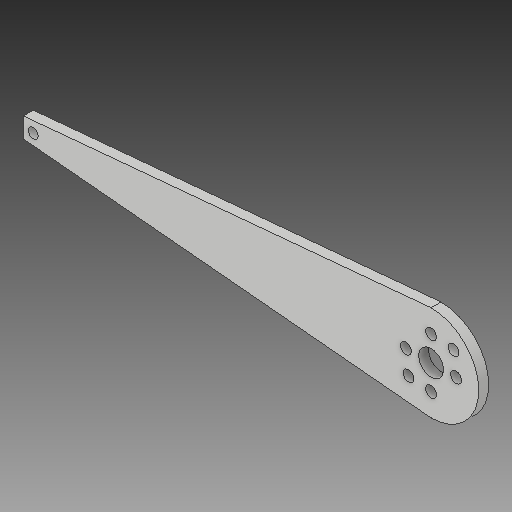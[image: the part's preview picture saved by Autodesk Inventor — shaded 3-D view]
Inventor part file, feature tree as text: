
AUTODESK INVENTOR PART (.ipt)
format: ipt  version: 2019 (Build 230136000, 136)  size: 179,200 bytes
history: native  units: in
note: dims shown in document units (in); Inventor stores cm internally (conversion verified against a paired STEP export)
features: extrude x11, sketch x9, plane x1
ambient origin geometry x8: Origin, YZ Plane, XZ Plane, XY Plane, X Axis, Y Axis, Z Axis, Center Point
bodies: Solid1 (feature_tree)
feature tree (21):
  sketch  "Sketch1"  dims[d0=1.2in d1=0.125in d2=0.0in]
  extrude  "Extrusion1"  Depth=0.125in TaperAngle=0.0deg
  sketch  "Sketch2"  dims[d3=0.125in d4=0.125in]
  plane  "Work Plane1"
  extrude  "Extrusion2"  Depth=0.125in
  extrude  "Extrusion3"  Depth=4.5295in TaperAngle=0.0deg
  extrude  "Extrusion4"  Depth=0.315in
  extrude  "Extrusion5"  Depth=0.315in
  extrude  "Extrusion7"  Depth=0.315in
  extrude  "Extrusion9"  Depth=0.138in
  sketch  "Sketch11"  dims[d18=0.138in d19=0.5in d20=0.0in]
  extrude  "Extrusion11"  Depth=0.5in TaperAngle=0.0deg
  extrude  "Extrusion12"  Depth=0.125in TaperAngle=0.0deg
  sketch  "Sketch12"  dims[d21=0.314in d22=0.5in d23=0.0in d26=0.125in d27=0.125in d28=0.125in d29=0.0in d37=0.4in d38=45.0deg d39=0.4in d40=0.138in d41=0.138in d42=1.0in d43=0.0in d47=1.0in d48=1.0in d49=0.0in d50=1.0in d51=1.0in d52=0.0in d53=0.125in d54=0.0in d55=0.125in d56=0.0in]
  extrude  "Extrusion13"  Depth=0.125in
  extrude  "Extrusion14"  Depth=0.125in
  sketch  "Sketch3"  dims[d6=0.25in d7=4.5295in d8=0.0in]
  sketch  "Sketch4"  dims[d9=0.5in d10=0.0in d11=0.315in]
  sketch  "Sketch5"  dims[d12=0.315in d13=0.315in]
  sketch  "Sketch7"  dims[d14=0.315in d15=0.138in]
  sketch  "Sketch9"  dims[d16=0.138in d17=0.138in]
